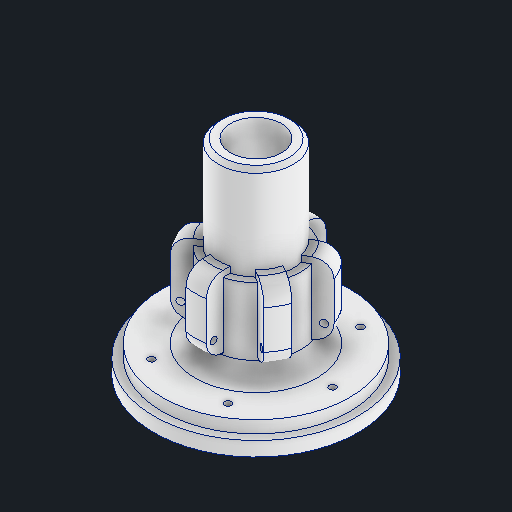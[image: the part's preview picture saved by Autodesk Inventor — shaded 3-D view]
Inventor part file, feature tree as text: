
AUTODESK INVENTOR PART (.ipt)
format: ipt  version: 2025.3 (Build 293356030, 356C)  size: 482,304 bytes
history: native  units: mm
features: sketch x15, extrude x7, fillet x3, pattern_circular x3, hole x3, plane x2, projected_geometry x2, chamfer x1
ambient origin geometry x8: Origin, YZ Plane, XZ Plane, XY Plane, X Axis, Y Axis, Z Axis, Center Point
bodies: Solid1 (feature_tree)
feature tree (36):
  sketch  "Sketch1"  dims[d1=25.0mm d2=5.8mm]
  extrude  "Extrusion1"  Depth=5.8mm
  extrude  "Extrusion2"  Depth=100.0mm TaperAngle=0.0deg
  plane  "Work Plane1"
  extrude  "Extrusion3"  Depth=10.0mm
  sketch  "Sketch3"  dims[d27=15.0mm d28=0.0mm]
  fillet  "Fillet2"  Radius=10.0mm
  pattern_circular  "Circular Pattern1"  Count=6 Angle=360.0deg
  plane  "Plano de trabajo2"
  extrude  "Extrusión5"  Depth=50.0mm TaperAngle=0.0deg
  extrude  "Extrusión6"  Depth=8.0mm
  fillet  "Empalme4"  Radius=60.0mm
  pattern_circular  "Patrón circular2"  Count=6 Angle=360.0deg
  chamfer  "Chaflán1"  Distance=6.0mm
  sketch  "Boceto6"  dims[d45=20.0mm d46=0.0mm d47=8.0mm d48=60.0mm d49=360.0deg]
  extrude  "Extrusión8"  Depth=8.0mm TaperAngle=360.0deg
  fillet  "Empalme6"  Radius=37.5mm
  hole  "Agujero4"  [1 undecoded]
  pattern_circular  "Patrón circular3"  [2 undecoded]
  extrude  "Extrusión9"  TaperAngle=30.0deg  [1 undecoded]
  hole  "Agujero5"  [1 undecoded]
  hole  "Agujero6"  [1 undecoded]
  sketch  "Boceto13"  dims[d97=31.0mm d98=7.5mm d99=2.459mm d100=9.0mm d101=4.0mm d102=2.0mm d103=90.0deg d104=9.0mm d105=120.0deg d106=30.0deg d107=37.5mm d108=60.0mm d110=360.0deg d112=3.4mm d113=6.0mm d114=4.0mm d115=2.0mm d116=90.0deg d117=8.0mm d118=20.594885mm d119=37.5mm d120=60.0mm d122=360.0deg d29=0.0mm d30=0.0mm d32=0.0mm d37=0.0mm]
  sketch  "Sketch2"  dims[d8=31.0mm d23=15.0mm d24=10.0mm]
  sketch  "Boceto4"  dims[d34=8.0mm d35=60.0mm d36=360.0deg]
  sketch  "Boceto5"  dims[d40=-46.0mm d42=50.0mm d43=0.0mm]
  projected_geometry  "Contorno proyectado1"
  sketch  "Boceto - Patrón circular1"  dims[d3=7.0mm d4=0.0mm d5=100.0mm d6=0.0mm]
  sketch  "Boceto8"  dims[d51=2.0mm d52=2.0mm d53=45.0deg]
  projected_geometry  "Contorno proyectado4"
  sketch  "Boceto9"  dims[d54=43.5mm d71=60.0mm d73=360.0deg d77=6.0mm d78=0.0mm]
  sketch  "Boceto10"  dims[d79=8.0mm]
  sketch  "Boceto11"  dims[d81=3.4mm d82=6.0mm d83=6.3mm d84=2.0mm d85=90.0deg d86=8.0mm d87=20.594885mm d88=60.0mm d89=360.0deg d91=37.5mm]
  sketch  "Boceto12"  dims[d92=25.74mm d94=4.0mm d95=0.0mm]
  sketch  "Boceto - Patrón circular2"  dims[d25=29.75mm]
  sketch  "Boceto - Patrón circular3"  dims[d31=3.0mm]
note: 6 required parameter values undecoded (feature->parameter linkage not recoverable at this tier; creation-order binding heuristic only, values carry confidence <= 0.55)
